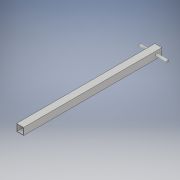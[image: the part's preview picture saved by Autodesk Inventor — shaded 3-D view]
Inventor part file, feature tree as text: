
AUTODESK INVENTOR PART (.ipt)
format: ipt  version: 2019.3 (Build 233278000, 278)  size: 113,664 bytes
history: native  units: mm
features: other x3, extrude x2, sketch x2, reference x2
ambient origin geometry x8: Origin, YZ Plane, XZ Plane, XY Plane, X Axis, Y Axis, Z Axis, Center Point
bodies: Solid1 (feature_tree)
feature tree (9):
  extrude  "Extrusion1"  Depth=22.225mm
  extrude  "Extrusion2"  Depth=500.0mm TaperAngle=0.0deg
  sketch  "Sketch1"  dims[d0=22.225mm d1=22.225mm]
  reference  "Reference1"
  reference  "Reference2"
  sketch  "Sketch2"  dims[d3=1.5875mm d8=500.0mm d9=0.0mm d10=8.0mm d11=12.7mm d12=19.05mm d13=40.0mm d14=60.0mm d15=0.0mm d16=0.0mm]
  parser-record x1  (decoder bookkeeping rows leaked as tree rows — omitted from the tree; the rows remain in map.json)
  other  "Assembly.iam"
  other  "RailMount:1"
note: 1 file-system path scrubbed to <path> (originals preserved in map.json)
